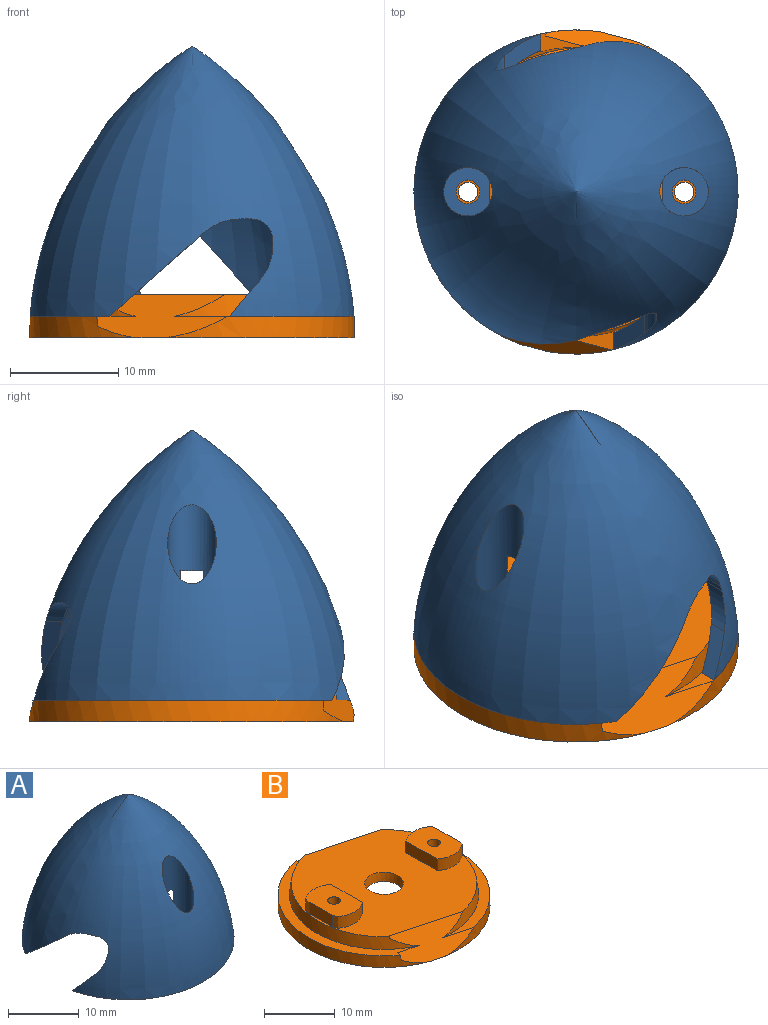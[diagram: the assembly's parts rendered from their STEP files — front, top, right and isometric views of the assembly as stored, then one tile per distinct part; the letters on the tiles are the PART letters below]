
ASSEMBLY  parts=2 mates=1
PART A: 33 faces, bbox 30.2x30.2x25.2 mm
  f0: plane 27.56x11.74mm, normal (0,0,-1), area 48.7mm2, adj f1,f2,f10,f22,f29
  f1: revolved ~30x30mm, area 1559.3mm2, adj f0,f3,f4,f8,f20,f21,f22,f23
  f2: revolved ~26.99x26.99mm, area 1045.8mm2, adj f0,f3,f5,f9,f10,f11,f20,f21
  f3: plane 27.66x11.55mm, normal (0,0,-1), area 48.9mm2, adj f1,f2,f9,f23,f28
  f4: cylinder r=2.25mm len=12.08mm, axis (0,0,-1), area 107.1mm2, adj f1,f7,f18,f19
  f5: cylinder r=4mm len=13.84mm, axis (0,0,-1), area 91.5mm2, adj f2,f6,f18,f19
  f6: plane 8x6mm, normal (0,0,-1), area 36.6mm2, adj f5,f9,f13,f19
  f7: plane 4.5x4.25mm, normal (0,0,1), area 11.8mm2, adj f4,f13,f19
  f8: cylinder r=2.25mm len=12.08mm, axis (0,0,-1), area 107.2mm2, adj f1,f15,f16,f17
  f9: cylinder r=4mm len=6.22mm, axis (0,0,-1), area 23.8mm2, adj f2,f3,f6
  f10: cylinder r=4mm len=6.22mm, axis (0,0,-1), area 23.8mm2, adj f0,f2,f12
  f11: cylinder r=4mm len=13.84mm, axis (0,0,-1), area 91.5mm2, adj f2,f12,f16,f17
  f12: plane 8x6mm, normal (0,0,-1), area 36.6mm2, adj f10,f11,f14,f16
  f13: cylinder r=1.1mm len=2.2mm, axis (0,0,-1), area 13.8mm2, adj f6,f7
  f14: cylinder r=1.1mm len=2.2mm, axis (0,0,-1), area 13.8mm2, adj f12,f15
  f15: plane 4.5x4.25mm, normal (0,0,1), area 11.8mm2, adj f8,f14,f16
  f16: plane 8x6.93mm, normal (0,-1,0), area 43.1mm2, adj f8,f11,f12,f15,f17
  f17: plane 6.93x2mm, normal (0,0,-1), area 9.5mm2, adj f8,f11,f16
  f18: plane 6.93x2mm, normal (0,0,-1), area 9.5mm2, adj f4,f5,f19
  f19: plane 8x6.93mm, normal (0,1,0), area 43.1mm2, adj f4,f5,f6,f7,f18
  f20: plane 2.25x1.07mm, normal (0,0,-1), area 1.9mm2, adj f1,f2,f24,f26
  f21: plane 2.09x0.41mm, normal (0,1,0), area 0.8mm2, adj f1,f2,f25,f26
  f22: plane 8.95x7.96mm, normal (0,-0.66,-0.75), area 18.8mm2, adj f0,f1,f2,f24
  f23: plane 3.48x3.31mm, normal (0,0.76,0.65), area 7.1mm2, adj f1,f2,f3,f25
  f24: cylinder r=5mm len=3.32mm, axis (1,0,0), area 6mm2, adj f1,f2,f20,f22
  f25: cylinder r=5mm len=3.47mm, axis (-1,0,0), area 6.4mm2, adj f1,f2,f21,f23
  f26: cylinder r=2mm len=2.49mm, axis (-1,0,0), area 6mm2, adj f1,f2,f20,f21
  f27: plane 2.42x2.05mm, normal (0,0,-1), area 3.5mm2, adj f1,f2,f31,f32
  f28: plane 7.51x6.72mm, normal (0,0.75,-0.67), area 16mm2, adj f1,f2,f3,f31
  f29: plane 4.97x3.94mm, normal (0,-0.82,0.57), area 9.5mm2, adj f0,f1,f2,f30
  f30: cylinder r=5mm len=3.41mm, axis (1,0,0), area 5.6mm2, adj f1,f2,f29,f32
  f31: cylinder r=5mm len=3.73mm, axis (1,0,0), area 6.8mm2, adj f1,f2,f27,f28
  f32: cylinder r=3mm len=2.76mm, axis (-1,0,0), area 5.6mm2, adj f1,f2,f27,f30
PART B: 33 faces, bbox 30x30x6 mm
  f0: cylinder r=15mm len=29.11mm, axis (0,0,-1), area 75mm2, adj f3,f5,f27,f28,f31,f32
  f1: cone r=13.4mm half-angle=7.5deg, axis (0,0,-1), area 65.4mm2, adj f2,f3,f28,f29,f30,f32
  f2: plane 26.27x25.64mm, normal (0,0,1), area 415mm2, adj f1,f6,f7,f9,f10,f12,f13,f14
  f3: plane 27.07x16.28mm, normal (0,0,1), area 55.8mm2, adj f0,f1,f27,f28,f31,f32
  f4: cylinder r=15mm len=28.93mm, axis (0,0,-1), area 74mm2, adj f5,f11,f28,f32
  f5: plane 30x30mm, normal (0,0,-1), area 568.7mm2, adj f0,f4,f15,f20,f25,f28,f32
  f6: cone r=13.4mm half-angle=7.5deg, axis (0,0,-1), area 65.3mm2, adj f2,f11,f28,f32
  f7: cone r=2.48mm half-angle=7.5deg, axis (0,0,1), area 25.1mm2, adj f2,f26
  f8: plane 8x5.27mm, normal (0,0,1), area 36.1mm2, adj f9,f12,f13,f14,f15,f16,f24
  f9: cylinder r=4mm len=5.02mm, axis (0,0,-1), area 10.8mm2, adj f2,f8,f16,f24
  f10: cylinder r=4mm len=5.12mm, axis (0,0,-1), area 11.1mm2, adj f2,f21,f22,f23
  f11: plane 26.82x16.62mm, normal (0,0,1), area 55.1mm2, adj f4,f6,f28,f32
  f12: plane 4.62x2mm, normal (-1,-0.01,0), area 9.2mm2, adj f2,f8,f13,f16
  f13: plane 2x0.76mm, normal (-0.94,-0.33,0), area 1.6mm2, adj f2,f8,f12,f14
  f14: cylinder r=4mm len=4.97mm, axis (0,0,-1), area 10.7mm2, adj f2,f8,f13,f24
  f15: cylinder r=0.9mm len=6mm, axis (0,0,-1), area 33.9mm2, adj f5,f8
  f16: plane 2x0.88mm, normal (-0.96,0.28,0), area 1.8mm2, adj f2,f8,f9,f12
  f17: plane 4.89x2mm, normal (1,0,0), area 9.8mm2, adj f2,f18,f21,f22
  f18: plane 2x0.7mm, normal (0.98,0.2,0), area 1.4mm2, adj f2,f17,f19,f22
  f19: cylinder r=4mm len=5.08mm, axis (0,0,-1), area 11mm2, adj f2,f18,f22,f23
  f20: cylinder r=0.9mm len=6mm, axis (0,0,-1), area 33.9mm2, adj f5,f22
  f21: plane 2x0.49mm, normal (0.98,-0.21,0), area 1mm2, adj f2,f10,f17,f22
  f22: plane 8x5.22mm, normal (0,0,1), area 36mm2, adj f10,f17,f18,f19,f20,f21,f23
  f23: plane 6.25x2mm, normal (-1,0,0), area 12.5mm2, adj f2,f10,f19,f22
  f24: plane 6.25x2mm, normal (1,0,0), area 12.5mm2, adj f2,f8,f9,f14
  f25: cylinder r=6.5mm len=13mm, axis (0,0,-1), area 102.1mm2, adj f5,f26
  f26: plane 13x13mm, normal (0,0,-1), area 112.5mm2, adj f7,f25
  f27: plane 0.93x0.81mm, normal (0.98,-0.15,0.13), area 0.3mm2, adj f0,f3,f28
  f28: plane 12.04x5.34mm, normal (-0.2,-0.74,0.64), area 47.6mm2, adj f0,f1,f2,f3,f4,f5,f6,f11
  f29: plane 0.24x0.21mm, normal (0.98,-0.15,0.13), area 0mm2, adj f1,f2,f28
  f30: plane 0.19x0.17mm, normal (0.98,-0.15,-0.13), area 0mm2, adj f1,f2,f32
  f31: plane 0.35x0.31mm, normal (0.98,-0.15,-0.13), area 0.1mm2, adj f0,f3,f32
  f32: plane 13.07x5.48mm, normal (0.2,0.74,0.64), area 50.2mm2, adj f0,f1,f2,f3,f4,f5,f6,f11
PLACE A rot(axis=(0,0,1),90deg) t=(-9.69,25.26,-6.22)mm
PLACE B t=(-9.69,25.26,-8.22)mm
MATE planar A.f14 <-> B.f9  axis (0,0,-1) through (-19.69,25.26,-2.22)mm
